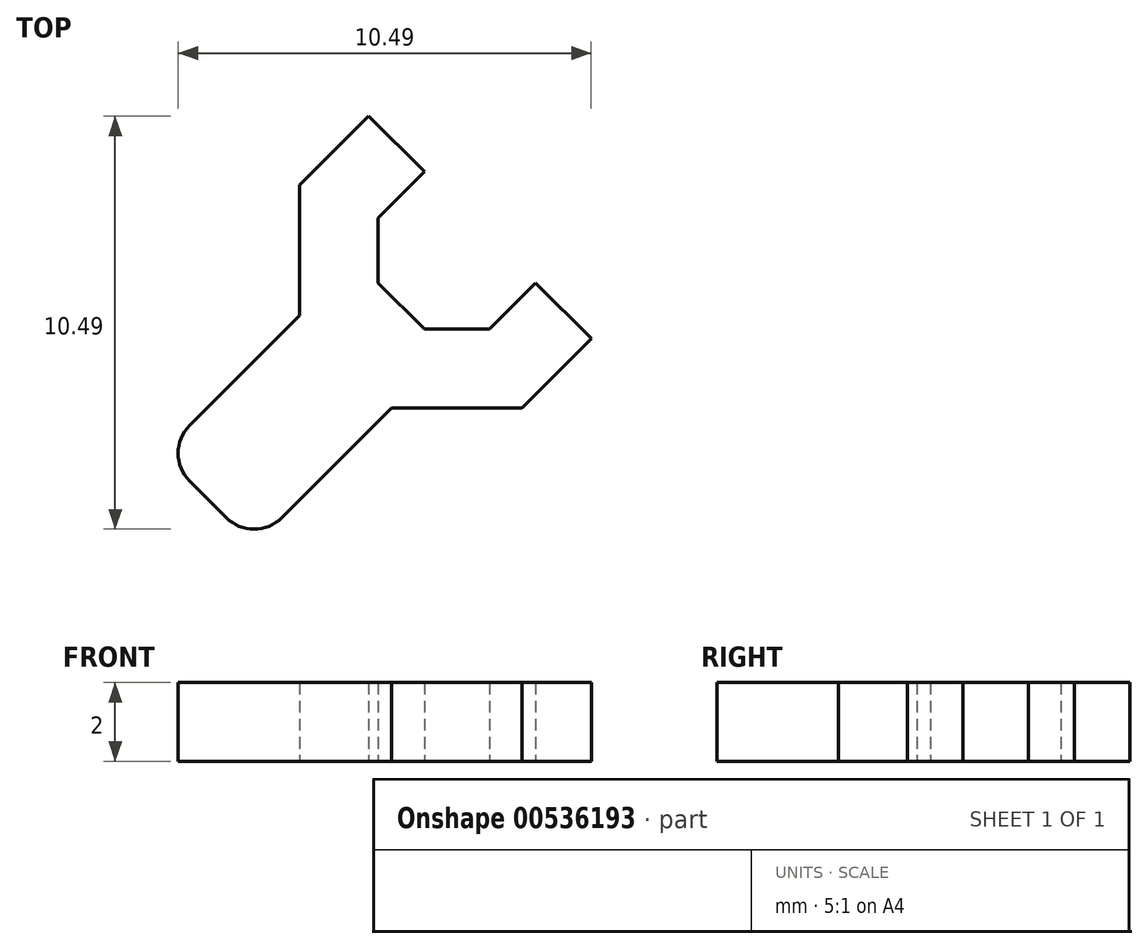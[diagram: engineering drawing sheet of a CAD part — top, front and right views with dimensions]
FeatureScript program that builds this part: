
annotation { "Feature Type Name" : "Feature", "Feature Type Description" : "" }
export const myFeature = defineFeature(function(context is Context, id is Id, definition is map)
    precondition{}
    {
        {
            var Q0;
            Q0=qCreatedBy(makeId("Top.planeOp"),FACE);
            var sketch = newSketch(context, id + "F0", { "sketchPlane" : qUnion([Q0])});
            skArc(sketch, "E0.cCircle", {"start": v(-1.41, 1.41) * mm, "mid": v(-1.41, -1.41) * mm, "end": v(1.41, -1.41) * mm, "construction": true});
            skLineSegment(sketch, "E0.1", {"start": v(2, -0.83) * mm, "end": v(0.83, -2) * mm});
            skLineSegment(sketch, "E0.2", {"start": v(0.83, -2) * mm, "end": v(-0.83, -2) * mm});
            skLineSegment(sketch, "E0.3", {"start": v(-0.83, -2) * mm, "end": v(-2, -0.83) * mm});
            skLineSegment(sketch, "E0.4", {"start": v(-2, -0.83) * mm, "end": v(-2, 0.83) * mm});
            skLineSegment(sketch, "E0.5", {"start": v(-2, 0.83) * mm, "end": v(-0.83, 2) * mm});
            skLineSegment(sketch, "E1.0", {"start": v(1.83, -2.41) * mm, "end": v(2.41, -1.83) * mm});
            skLineSegment(sketch, "E2.0", {"start": v(-4, 1.66) * mm, "end": v(-2.24, 3.41) * mm});
            skLineSegment(sketch, "E2.1", {"start": v(3.41, -2.24) * mm, "end": v(1.66, -4) * mm});
            skLineSegment(sketch, "E2.2", {"start": v(1.66, -4) * mm, "end": v(-1.66, -4) * mm});
            skLineSegment(sketch, "E2.4", {"start": v(-4, -1.66) * mm, "end": v(-4, 1.66) * mm});
            skLineSegment(sketch, "E3", {"start": v(-2.24, 3.41) * mm, "end": v(-0.83, 2) * mm});
            skLineSegment(sketch, "E4", {"start": v(2, -0.83) * mm, "end": v(3.41, -2.24) * mm});
            skLineSegment(sketch, "E5", {"start": v(-4, -1.66) * mm, "end": v(-6.79, -4.45) * mm});
            skLineSegment(sketch, "E6", {"start": v(-6.79, -5.86) * mm, "end": v(-5.86, -6.79) * mm});
            skLineSegment(sketch, "E7", {"start": v(-4.45, -6.79) * mm, "end": v(-1.66, -4) * mm});
            skPoint(sketch, "E8.visualSharp", {"position": v(-7.5, -5.15) * mm});
            skArc(sketch, "E8.filletArc", {"start": v(-6.79, -4.45) * mm, "mid": v(-7.08, -5.15) * mm, "end": v(-6.79, -5.86) * mm});
            skPoint(sketch, "E9.visualSharp", {"position": v(-5.15, -7.5) * mm});
            skArc(sketch, "E9.filletArc", {"start": v(-5.86, -6.79) * mm, "mid": v(-5.15, -7.08) * mm, "end": v(-4.45, -6.79) * mm});
            skSolve(sketch);
        }
        {
            var Q0;
            Q0 = qSketchRegion(id + "F0", true);
            extrude(context, id + "F1", {"entities" : qUnion([Q0]), "depth" : 2 * mm, "offsetDistance" : 25 * mm});
        }
    });
